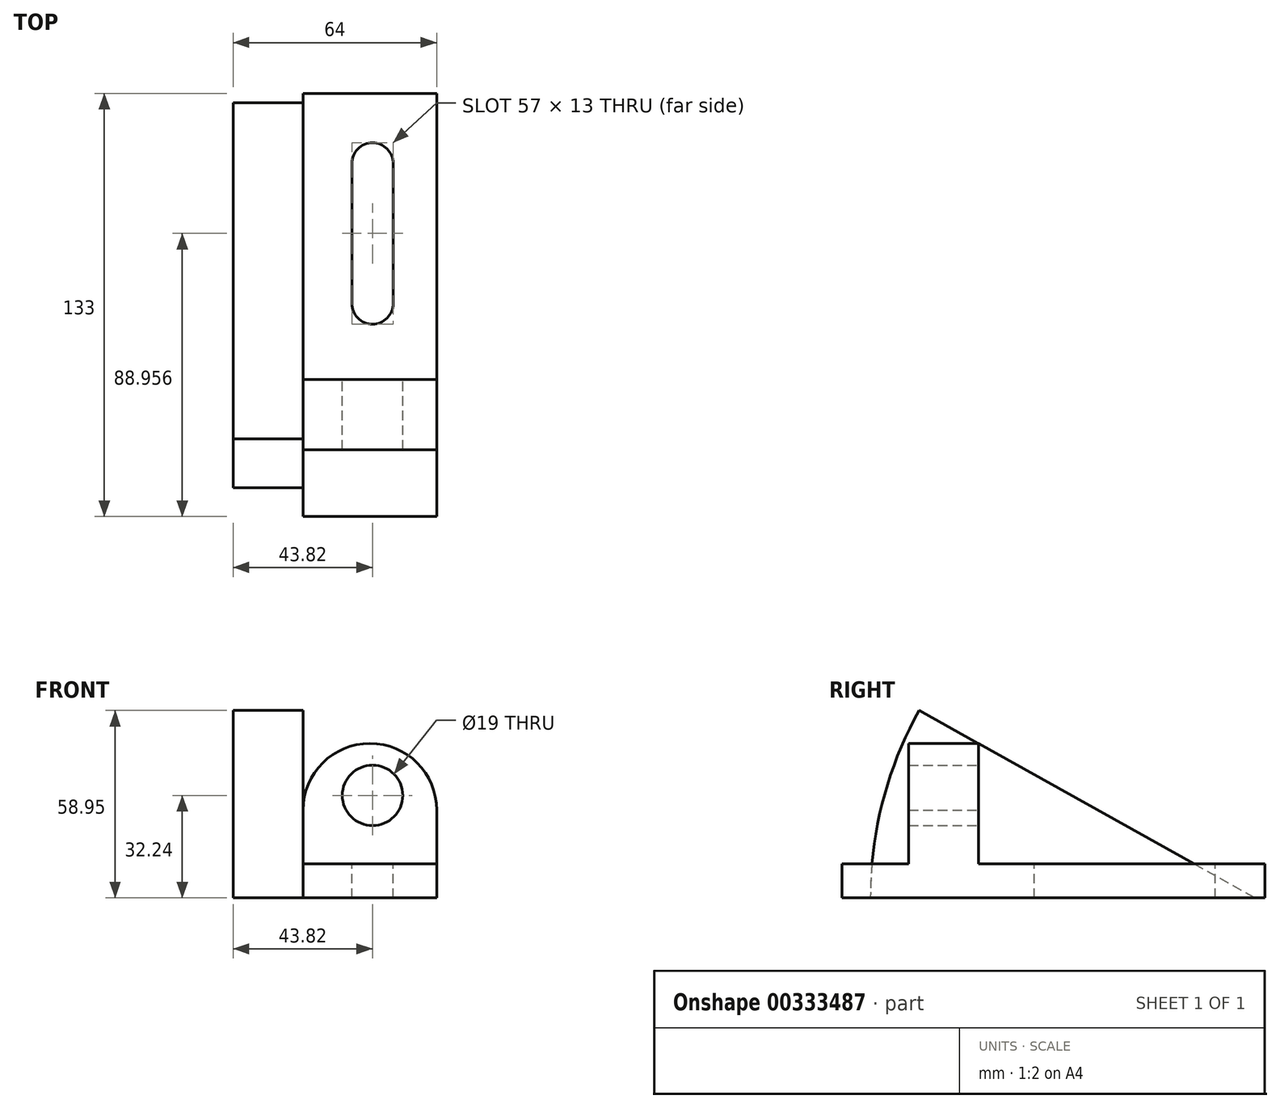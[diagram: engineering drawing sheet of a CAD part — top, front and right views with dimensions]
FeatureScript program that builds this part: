
annotation { "Feature Type Name" : "Feature", "Feature Type Description" : "" }
export const myFeature = defineFeature(function(context is Context, id is Id, definition is map)
    precondition{}
    {
        {
            var Q0;
            Q0=qCreatedBy(makeId("Front.planeOp"),FACE);
            var sketch = newSketch(context, id + "F0", { "sketchPlane" : qUnion([Q0])});
            skLineSegment(sketch, "E0", {"start": v(-21.82, 0) * mm, "end": v(20.18, 0) * mm});
            skLineSegment(sketch, "E1", {"start": v(20.18, 0) * mm, "end": v(20.18, 16) * mm});
            skLineSegment(sketch, "E2", {"start": v(20.18, 16) * mm, "end": v(-21.82, 16) * mm});
            skLineSegment(sketch, "E3", {"start": v(-21.82, 16) * mm, "end": v(-21.82, 0) * mm});
            skLineSegment(sketch, "E4", {"start": v(-21.82, 16) * mm, "end": v(-21.82, 27.6) * mm});
            skLineSegment(sketch, "E5", {"start": v(20.18, 27.6) * mm, "end": v(20.18, 16) * mm});
            skArc(sketch, "E6", {"start": v(20.18, 27.6) * mm, "mid": v(-0.82, 48.6) * mm, "end": v(-21.82, 27.6) * mm});
            skSolve(sketch);
        }
        {
            var Q0;
            Q0 = qSketchRegion(id + "F0", true);
            extrude(context, id + "F1", {"entities" : qUnion([Q0]), "depth" : 133 * mm});
        }
        {
            var Q0;
            Q0=qCreatedBy(makeId("Right.planeOp"),FACE);
            var sketch = newSketch(context, id + "F2", { "sketchPlane" : qUnion([Q0])});
            skLineSegment(sketch, "E7", {"start": v(-133, 0) * mm, "end": v(-112, 0) * mm});
            skLineSegment(sketch, "E8", {"start": v(-112, 0) * mm, "end": v(-112, 63.5) * mm});
            skLineSegment(sketch, "E9", {"start": v(-112, 63.5) * mm, "end": v(-133, 63.5) * mm});
            skLineSegment(sketch, "E10", {"start": v(-133, 63.5) * mm, "end": v(-133, 0) * mm});
            skLineSegment(sketch, "E11", {"start": v(-133, 10.7) * mm, "end": v(-112, 10.7) * mm});
            skSolve(sketch);
        }
        {
            var Q0;
            {var subQ0=sQuery(id+"F2.wireOp",EDGE,"E9");Q0=makeQuery(id+"F2.imprint","IMPRINT",FACE,{"disambiguationData":[TD([[makeQuery(id+"F2.imprint","IMPRINT",EDGE,{"derivedFrom":subQ0}),1.0]])]});}
            extrude(context, id + "F3", {"entities" : qUnion([Q0]), "operationType" : NewBodyOperationType.REMOVE, "endBound" : BoundingType.THROUGH_ALL, "depth" : 25 * mm});
        }
        {
            var Q0;
            Q0=makeQuery(id+"F3.boolean.opBoolean","COPY",FACE,{"derivedFrom":makeQuery(id+"F3.opExtrude","CAP_FACE",FACE,{"disambiguationData":[OSD([sQuery(id+"F2.wireOp",EDGE,"E8"),sQuery(id+"F2.wireOp",EDGE,"E9"),sQuery(id+"F2.wireOp",EDGE,"E10"),sQuery(id+"F2.wireOp",EDGE,"E11")])],"isStart":true})});
            var sketch = newSketch(context, id + "F4", { "sketchPlane" : qUnion([Q0])});
            skLineSegment(sketch, "E12", {"start": v(-112, 10.7) * mm, "end": v(-133, 10.7) * mm});
            skLineSegment(sketch, "E13", {"start": v(-133, 10.7) * mm, "end": v(-133, 51.3) * mm});
            skLineSegment(sketch, "E14", {"start": v(-133, 51.3) * mm, "end": v(-112, 51.3) * mm});
            skLineSegment(sketch, "E15", {"start": v(-112, 51.3) * mm, "end": v(-112, 10.7) * mm});
            skSolve(sketch);
        }
        {
            var Q0;
            Q0 = qSketchRegion(id + "F4", true);
            extrude(context, id + "F5", {"entities" : qUnion([Q0]), "operationType" : NewBodyOperationType.REMOVE, "oppositeDirection" : true, "depth" : 25 * mm});
        }
        {
            var Q0;
            Q0=qCreatedBy(makeId("Right.planeOp"),FACE);
            var sketch = newSketch(context, id + "F6", { "sketchPlane" : qUnion([Q0])});
            skPoint(sketch, "E16", {"position": v(-112, 10.7) * mm});
            skPoint(sketch, "E17", {"position": v(-90, 10.7) * mm});
            skLineSegment(sketch, "E18", {"start": v(-90, 10.7) * mm, "end": v(-90, 56.6) * mm});
            skLineSegment(sketch, "E19", {"start": v(-90, 56.6) * mm, "end": v(0, 56.6) * mm});
            skLineSegment(sketch, "E20", {"start": v(0, 56.6) * mm, "end": v(0, 10.7) * mm});
            skLineSegment(sketch, "E21", {"start": v(0, 10.7) * mm, "end": v(-90, 10.7) * mm});
            skSolve(sketch);
        }
        {
            var Q0;
            Q0 = qSketchRegion(id + "F6", true);
            extrude(context, id + "F7", {"entities" : qUnion([Q0]), "operationType" : NewBodyOperationType.REMOVE, "endBound" : BoundingType.THROUGH_ALL, "depth" : 25 * mm, "hasSecondDirection" : true, "secondDirectionOppositeDirection" : true, "secondDirectionDepth" : 25 * mm});
        }
        {
            var Q0;
            Q0=makeQuery(id+"F7.boolean.opBoolean","COPY",FACE,{"derivedFrom":makeQuery(id+"F7.opExtrude","SWEPT_FACE",FACE,{"disambiguationData":[OSD([sQuery(id+"F6.wireOp",EDGE,"E21")])]})});
            var sketch = newSketch(context, id + "F8", { "sketchPlane" : qUnion([Q0])});
            skPoint(sketch, "E22", {"position": v(0, -22.04) * mm});
            skPoint(sketch, "E23", {"position": v(0, -66.04) * mm});
            skLineSegment(sketch, "E24", {"start": v(-6.5, -22.04) * mm, "end": v(-6.5, -66.04) * mm});
            skLineSegment(sketch, "E25", {"start": v(6.5, -22.04) * mm, "end": v(6.5, -66.04) * mm});
            skArc(sketch, "E26", {"start": v(6.5, -22.04) * mm, "mid": v(0, -15.54) * mm, "end": v(-6.5, -22.04) * mm});
            skArc(sketch, "E27", {"start": v(-6.5, -66.04) * mm, "mid": v(0, -72.54) * mm, "end": v(6.5, -66.04) * mm});
            skSolve(sketch);
        }
        {
            var Q0;
            Q0=makeQuery(id+"F7.boolean.opBoolean","COPY",FACE,{"derivedFrom":makeQuery(id+"F7.opExtrude","SWEPT_FACE",FACE,{"disambiguationData":[OSD([sQuery(id+"F6.wireOp",EDGE,"E18")])]})});
            var sketch = newSketch(context, id + "F9", { "sketchPlane" : qUnion([Q0])});
            skPoint(sketch, "E28", {"position": v(0, 32.24) * mm});
            skSolve(sketch);
        }
        {
            var Q0;
            Q0=makeQuery(id+"F1.opExtrude","SWEPT_FACE",FACE,{"disambiguationData":[OSD([sQuery(id+"F0.wireOp",EDGE,"E3"),sQuery(id+"F0.wireOp",EDGE,"E4")])]});
            var sketch = newSketch(context, id + "F10", { "sketchPlane" : qUnion([Q0])});
            skArc(sketch, "E29", {"start": v(108.67, 58.95) * mm, "mid": v(120.1, 30.45) * mm, "end": v(124, 0) * mm});
            skLineSegment(sketch, "E30", {"start": v(108.67, 58.95) * mm, "end": v(3, 0) * mm});
            skSolve(sketch);
        }
        {
            var Q0;
            Q0 = qSketchRegion(id + "F10", true);
            var Q1;
            {var subQ0=sQuery(id+"F0.wireOp",EDGE,"E4");Q1=makeQuery(id+"F10.imprint","IMPRINT",FACE,{"disambiguationData":[TD([[makeQuery(id+"F10.imprint","IMPRINT",EDGE,{"derivedFrom":makeQuery(id+"F1.opExtrude","SWEPT_EDGE",EDGE,{"disambiguationData":[OSD([subQ0,sQuery(id+"F0.wireOp",EDGE,"E6")])]})}),-1.0]])]});}
            var Q2;
            {var subQ0=sQuery(id+"F0.wireOp",EDGE,"E4");Q2=makeQuery(id+"F10.imprint","IMPRINT",FACE,{"disambiguationData":[TD([[makeQuery(id+"F10.imprint","IMPRINT",EDGE,{"derivedFrom":makeQuery(id+"F1.opExtrude","SWEPT_EDGE",EDGE,{"disambiguationData":[OSD([subQ0,sQuery(id+"F0.wireOp",EDGE,"E6")])]})}),1.0]])]});}
            extrude(context, id + "F11", {"entities" : qUnion([Q0, Q1, Q2]), "operationType" : NewBodyOperationType.ADD, "depth" : 22 * mm});
        }
        {
            var Q0;
            {var subQ0=sQuery(id+"F6.wireOp",EDGE,"E18");Q0=makeQuery(id+"F9.imprint","IMPRINT",FACE,{"disambiguationData":[TD([[makeQuery(id+"F9.imprint","IMPRINT",EDGE,{"derivedFrom":makeQuery(id+"F7.boolean.opBoolean","COPY",EDGE,{"derivedFrom":makeQuery(id+"F7.opExtrude","SWEPT_EDGE",EDGE,{"disambiguationData":[OSD([subQ0,sQuery(id+"F6.wireOp",EDGE,"E21")])]})})}),1.0]])]});}
            var sketch = newSketch(context, id + "F12", { "sketchPlane" : qUnion([Q0])});
            skCircle(sketch, "E31", {"center": v(0, 32.24) * mm, "radius": 9.5 * mm});
            skSolve(sketch);
        }
        {
            var Q0;
            Q0 = qSketchRegion(id + "F8", true);
            extrude(context, id + "F13", {"entities" : qUnion([Q0]), "operationType" : NewBodyOperationType.REMOVE, "oppositeDirection" : true, "depth" : 25 * mm});
        }
        {
            var Q0;
            Q0 = qSketchRegion(id + "F12", true);
            extrude(context, id + "F14", {"entities" : qUnion([Q0]), "operationType" : NewBodyOperationType.REMOVE, "oppositeDirection" : true, "depth" : 25 * mm});
        }
    });
